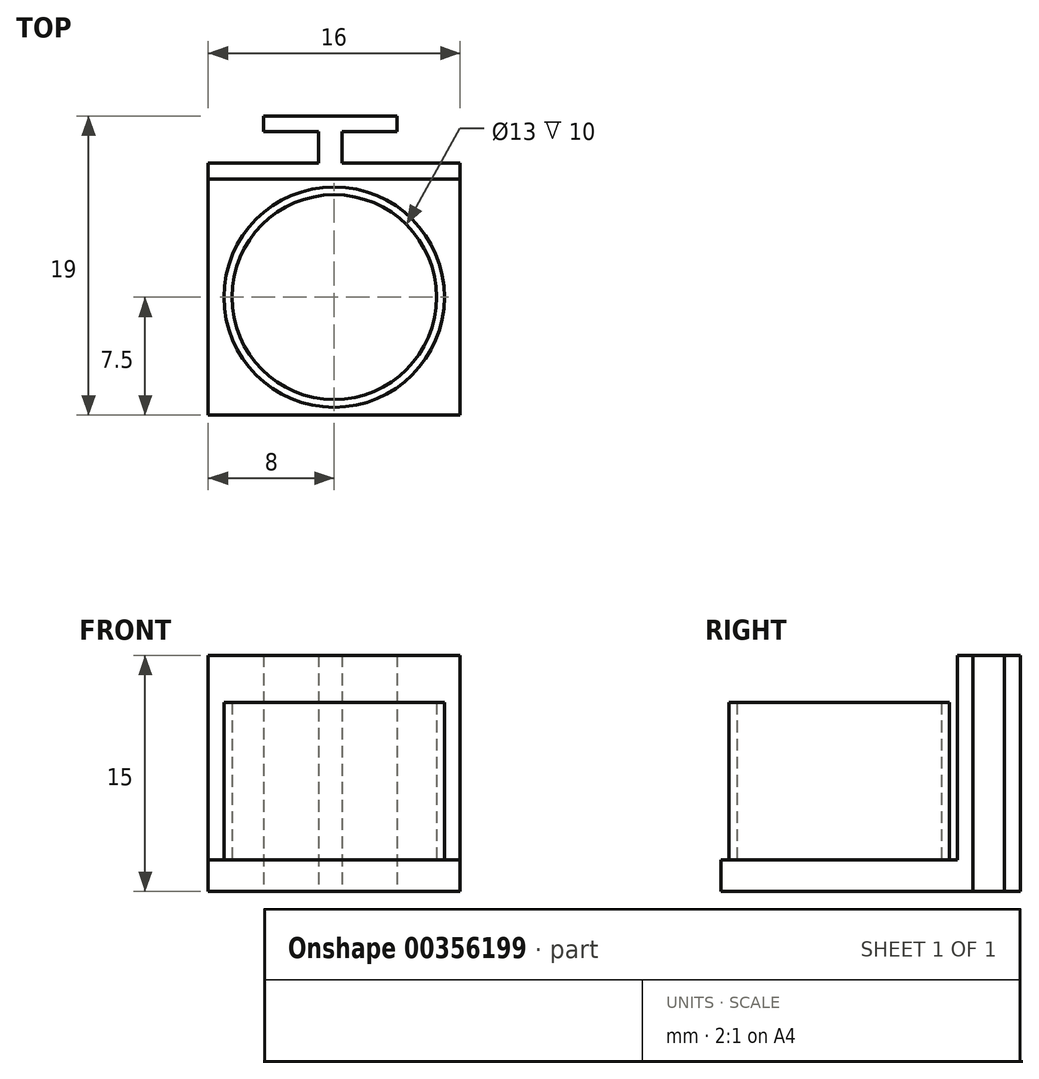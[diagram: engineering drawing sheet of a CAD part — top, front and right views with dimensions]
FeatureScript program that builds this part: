
annotation { "Feature Type Name" : "Feature", "Feature Type Description" : "" }
export const myFeature = defineFeature(function(context is Context, id is Id, definition is map)
    precondition{}
    {
        {
            var Q0;
            Q0=qCreatedBy(makeId("Top.planeOp"),FACE);
            var sketch = newSketch(context, id + "F0", { "sketchPlane" : qUnion([Q0])});
            skLineSegment(sketch, "E0.bottom", {"start": v(0, 0) * mm, "end": v(9, 0) * mm});
            skLineSegment(sketch, "E0.top", {"start": v(0, 6) * mm, "end": v(9, 6) * mm});
            skLineSegment(sketch, "E0.left", {"start": v(0, 0) * mm, "end": v(0, 6) * mm});
            skLineSegment(sketch, "E0.right", {"start": v(9, 0) * mm, "end": v(9, 6) * mm});
            skPoint(sketch, "E1", {"position": v(4.5, 6) * mm});
            skPoint(sketch, "E2", {"position": v(5.25, 6) * mm});
            skPoint(sketch, "E3", {"position": v(3.75, 6) * mm});
            skLineSegment(sketch, "E4", {"start": v(5.25, 6) * mm, "end": v(3.75, 6) * mm});
            skLineSegment(sketch, "E5", {"start": v(3.75, 6) * mm, "end": v(3.75, 8) * mm});
            skLineSegment(sketch, "E6", {"start": v(3.75, 8) * mm, "end": v(5.25, 8) * mm});
            skLineSegment(sketch, "E7", {"start": v(5.25, 8) * mm, "end": v(5.25, 6) * mm});
            skLineSegment(sketch, "E8", {"start": v(5.25, 8) * mm, "end": v(8.75, 8) * mm});
            skLineSegment(sketch, "E9", {"start": v(8.75, 8) * mm, "end": v(8.75, 9) * mm});
            skLineSegment(sketch, "E10", {"start": v(8.75, 9) * mm, "end": v(0.25, 9) * mm});
            skLineSegment(sketch, "E11", {"start": v(0.25, 9) * mm, "end": v(0.25, 8) * mm});
            skLineSegment(sketch, "E12", {"start": v(0.25, 8) * mm, "end": v(3.75, 8) * mm});
            skSolve(sketch);
        }
        {
            var Q0;
            {var subQ2=sQuery(id+"F0.wireOp",EDGE,"E5");Q0=makeQuery(id+"F0.imprint","IMPRINT",FACE,{"disambiguationData":[TD([[makeQuery(id+"F0.imprint","IMPRINT",EDGE,{"derivedFrom":subQ2}),-1.0]])]});}
            var Q1;
            Q1=makeQuery(id+"F0.imprint","IMPRINT",FACE,{"disambiguationData":[TD([[makeQuery(id+"F0.imprint","IMPRINT",EDGE,{"derivedFrom":sQuery(id+"F0.wireOp",EDGE,"E6")}),1.0]])]});
            extrude(context, id + "F1", {"entities" : qUnion([Q0, Q1]), "depth" : 15 * mm, "offsetDistance" : 25 * mm});
        }
        {
            var Q0;
            Q0=makeQuery(id+"F1.opExtrude","SWEPT_FACE",FACE,{"disambiguationData":[OSD([sQuery(id+"F0.wireOp",EDGE,"E0.top")])]});
            var sketch = newSketch(context, id + "F2", { "sketchPlane" : qUnion([Q0])});
            skLineSegment(sketch, "E13", {"start": v(3.75, 15) * mm, "end": v(12.75, 15) * mm});
            skLineSegment(sketch, "E14", {"start": v(3.75, 15) * mm, "end": v(-3.25, 15) * mm});
            skLineSegment(sketch, "E15", {"start": v(-3.25, 15) * mm, "end": v(-3.25, 0) * mm});
            skLineSegment(sketch, "E16", {"start": v(-3.25, 0) * mm, "end": v(12.75, 0) * mm});
            skLineSegment(sketch, "E17", {"start": v(12.75, 0) * mm, "end": v(12.75, 15) * mm});
            skSolve(sketch);
        }
        {
            var Q0;
            Q0 = qSketchRegion(id + "F2", true);
            extrude(context, id + "F3", {"entities" : qUnion([Q0]), "operationType" : NewBodyOperationType.ADD, "depth" : 1 * mm, "offsetDistance" : 25 * mm});
        }
        {
            var Q0;
            Q0=makeQuery(id+"F3.opExtrude","CAP_FACE",FACE,{"disambiguationData":[OSD([sQuery(id+"F2.wireOp",EDGE,"E13"),sQuery(id+"F2.wireOp",EDGE,"E14"),sQuery(id+"F2.wireOp",EDGE,"E15"),sQuery(id+"F2.wireOp",EDGE,"E16"),sQuery(id+"F2.wireOp",EDGE,"E17")])],"isStart":false});
            var sketch = newSketch(context, id + "F4", { "sketchPlane" : qUnion([Q0])});
            skLineSegment(sketch, "E18", {"start": v(-3.25, 0) * mm, "end": v(-3.25, 2) * mm});
            skLineSegment(sketch, "E19", {"start": v(-3.25, 2) * mm, "end": v(12.75, 2) * mm});
            skLineSegment(sketch, "E20", {"start": v(12.75, 2) * mm, "end": v(12.75, 0) * mm});
            skLineSegment(sketch, "E21", {"start": v(12.75, 0) * mm, "end": v(-3.25, 0) * mm});
            skSolve(sketch);
        }
        {
            var Q0;
            Q0 = qSketchRegion(id + "F4", true);
            extrude(context, id + "F5", {"entities" : qUnion([Q0]), "operationType" : NewBodyOperationType.ADD, "depth" : 15 * mm, "offsetDistance" : 25 * mm});
        }
        {
            var Q0;
            Q0=makeQuery(id+"F5.opExtrude","SWEPT_FACE",FACE,{"disambiguationData":[OSD([sQuery(id+"F4.wireOp",EDGE,"E19")])]});
            var sketch = newSketch(context, id + "F6", { "sketchPlane" : qUnion([Q0])});
            skPoint(sketch, "E22", {"position": v(4.75, 5) * mm});
            skPoint(sketch, "E23", {"position": v(12.75, -2.5) * mm});
            skPoint(sketch, "E24", {"position": v(4.75, -2.5) * mm});
            skCircle(sketch, "E25", {"center": v(4.75, -2.5) * mm, "radius": 7 * mm});
            skCircle(sketch, "E26", {"center": v(4.75, -2.5) * mm, "radius": 6.5 * mm});
            skSolve(sketch);
        }
        {
            var Q0;
            Q0=makeQuery(id+"F6.imprint","IMPRINT",FACE,{"disambiguationData":[TD([[makeQuery(id+"F6.imprint","IMPRINT",EDGE,{"derivedFrom":sQuery(id+"F6.wireOp",EDGE,"E25")}),1.0]])]});
            extrude(context, id + "F7", {"entities" : qUnion([Q0]), "operationType" : NewBodyOperationType.ADD, "depth" : 10 * mm, "offsetDistance" : 25 * mm});
        }
    });
